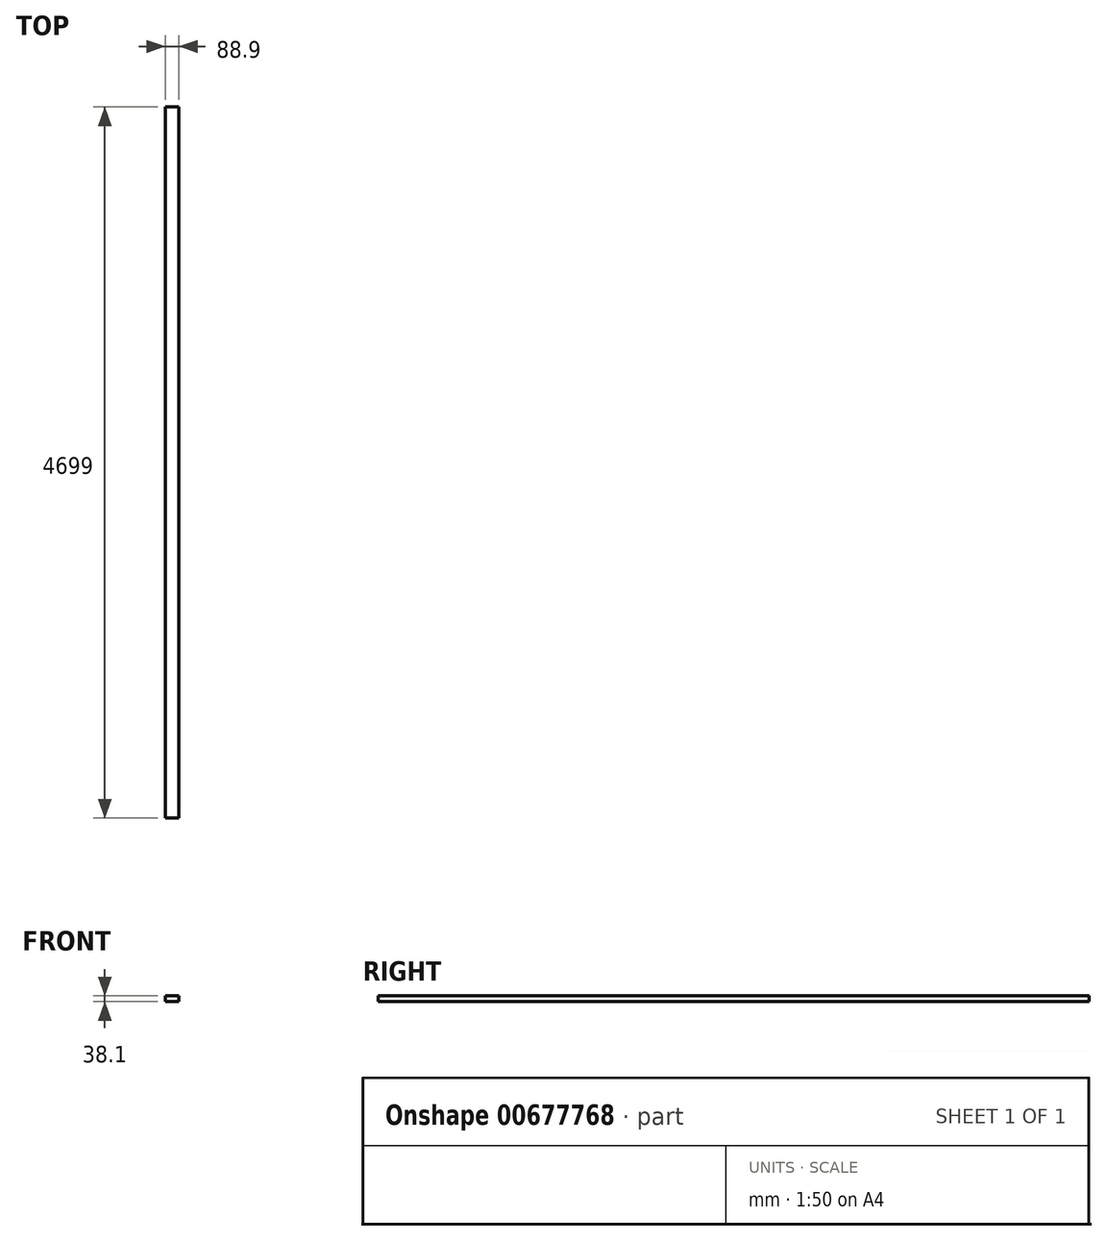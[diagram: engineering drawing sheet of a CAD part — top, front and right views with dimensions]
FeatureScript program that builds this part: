
annotation { "Feature Type Name" : "Feature", "Feature Type Description" : "" }
export const myFeature = defineFeature(function(context is Context, id is Id, definition is map)
    precondition{}
    {
        {
            var Q0;
            Q0=qCreatedBy(makeId("Front.planeOp"),FACE);
            var sketch = newSketch(context, id + "F0", { "sketchPlane" : qUnion([Q0])});
            skLineSegment(sketch, "E0.bottom", {"start": v(77.44, 0) * mm, "end": v(166.34, 0) * mm});
            skLineSegment(sketch, "E0.top", {"start": v(77.44, -38.1) * mm, "end": v(166.34, -38.1) * mm});
            skLineSegment(sketch, "E0.left", {"start": v(77.44, 0) * mm, "end": v(77.44, -38.1) * mm});
            skLineSegment(sketch, "E0.right", {"start": v(166.34, 0) * mm, "end": v(166.34, -38.1) * mm});
            skSolve(sketch);
        }
        {
            var Q0;
            Q0=makeQuery(id+"F0.imprint","IMPRINT",FACE,{"disambiguationData":[TD([[makeQuery(id+"F0.imprint","IMPRINT",EDGE,{"derivedFrom":sQuery(id+"F0.wireOp",EDGE,"E0.bottom")}),-1.0]])]});
            extrude(context, id + "F1", {"entities" : qUnion([Q0]), "depth" : 4699 * mm, "offsetDistance" : 25.4 * mm});
        }
    });
